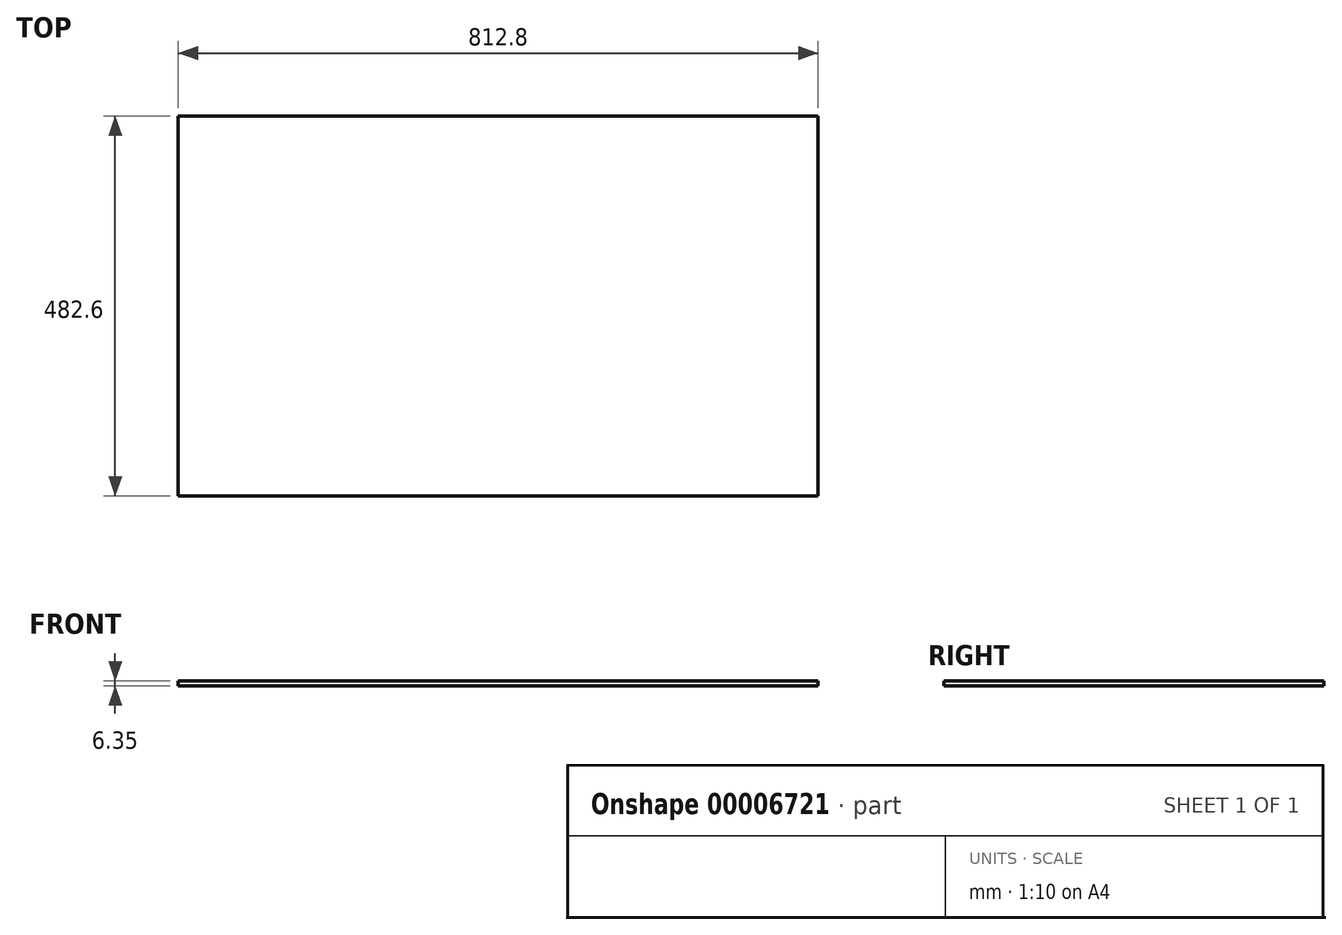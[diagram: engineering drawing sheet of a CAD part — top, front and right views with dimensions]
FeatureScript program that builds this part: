
annotation { "Feature Type Name" : "Feature", "Feature Type Description" : "" }
export const myFeature = defineFeature(function(context is Context, id is Id, definition is map)
    precondition{}
    {
        {
            var Q0;
            Q0=qCreatedBy(makeId("Top.planeOp"),FACE);
            var sketch = newSketch(context, id + "F0", { "sketchPlane" : qUnion([Q0])});
            skLineSegment(sketch, "E0.bottom", {"start": v(-495.3, 25.4) * mm, "end": v(317.5, 25.4) * mm});
            skLineSegment(sketch, "E0.top", {"start": v(-495.3, -457.2) * mm, "end": v(317.5, -457.2) * mm});
            skLineSegment(sketch, "E0.left", {"start": v(-495.3, 25.4) * mm, "end": v(-495.3, -457.2) * mm});
            skLineSegment(sketch, "E0.right", {"start": v(317.5, 25.4) * mm, "end": v(317.5, -457.2) * mm});
            skSolve(sketch);
        }
        {
            var Q0;
            Q0=makeQuery(id+"F0.imprint","IMPRINT",FACE,{"disambiguationData":[TD([[makeQuery(id+"F0.imprint","IMPRINT",EDGE,{"derivedFrom":sQuery(id+"F0.wireOp",EDGE,"E0.bottom")}),-1.0]])]});
            extrude(context, id + "F1", {"entities" : qUnion([Q0]), "depth" : 6.35 * mm});
        }
    });
